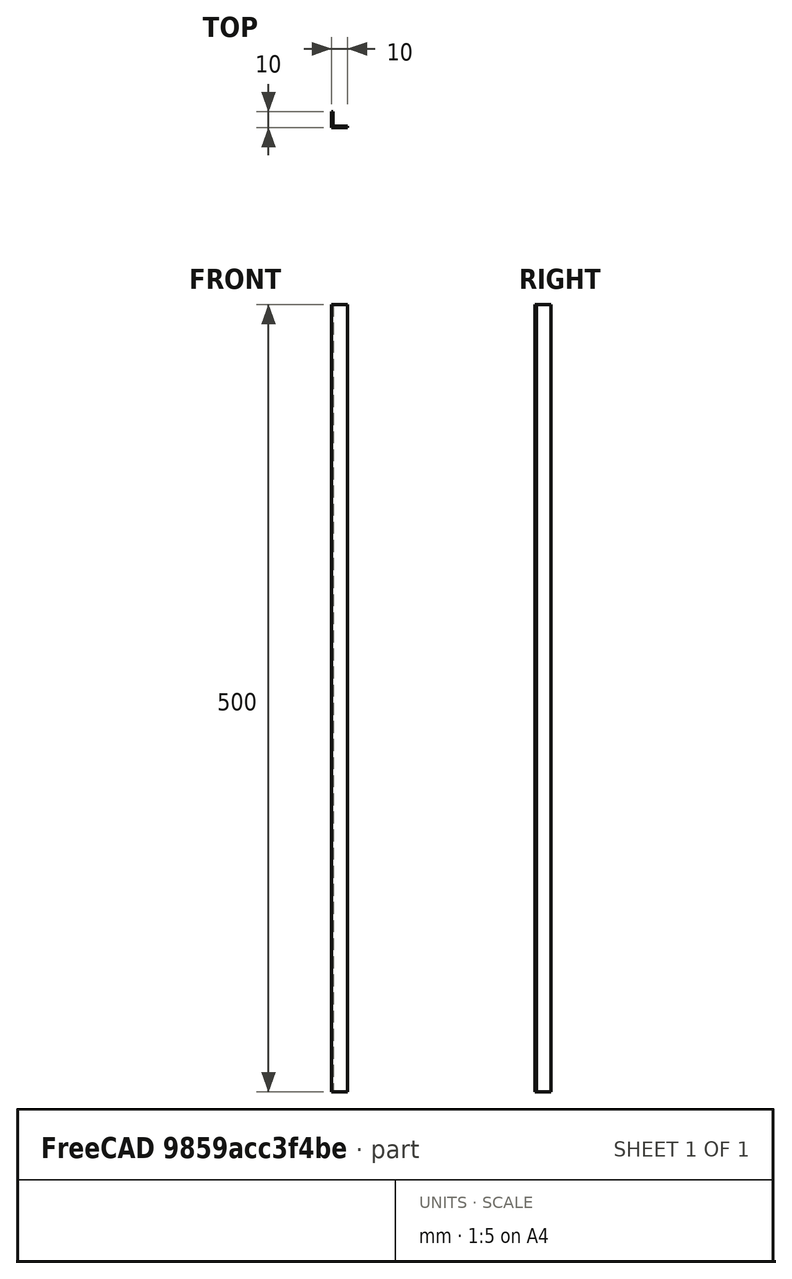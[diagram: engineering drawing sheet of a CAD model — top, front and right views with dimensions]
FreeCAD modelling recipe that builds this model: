
FCSTD DOCUMENT  (FreeCAD 0.18R16131 (Git))
Label: norm_L-profile_10_10_1_500
License: All rights reserved
LicenseURL: http://en.wikipedia.org/wiki/All_rights_reserved
objects: Sketcher::SketchObject×1, PartDesign::Pad×1, PartDesign::Body×1, Spreadsheet::Sheet×1
note: 4 computed .brp shape members not serialized (recipe doc carries the construction recipe); baked Part::Feature solids carry a one-line shape summary decoded from their .brp

FEATURE [Sketcher::SketchObject] Sketch
  MapMode = 5
  Support = -> [XY_Plane]
  expr: Constraints[17] = Lprofile.t1
  expr: Constraints[14] = Lprofile.d2
  expr: Constraints[16] = Lprofile.d1
  sketch-geometry (6):
    g0: LineSegment StartX=0 StartY=0 StartZ=0 EndX=0 EndY=9 EndZ=0
    g1: LineSegment StartX=0 StartY=9 StartZ=0 EndX=-1 EndY=9 EndZ=0
    g2: LineSegment StartX=-1 StartY=9 StartZ=0 EndX=-1 EndY=-1 EndZ=0
    g3: LineSegment StartX=-1 StartY=-1 StartZ=0 EndX=9 EndY=-1 EndZ=0
    g4: LineSegment StartX=9 StartY=-1 StartZ=0 EndX=9 EndY=0 EndZ=0
    g5: LineSegment StartX=9 StartY=0 StartZ=0 EndX=0 EndY=0 EndZ=0
  constraints (18):
    c: PointOnObject(g0,g-2)
    c: Vertical(g0)
    c: Coincident(g1,g0)
    c: Horizontal(g1)
    c: Coincident(g2,g1)
    c: Vertical(g2)
    c: Coincident(g3,g2)
    c: Horizontal(g3)
    c: PointOnObject(g4,g-1)
    c: Vertical(g4)
    c: Coincident(g5,g4)
    c: Coincident(g5,g0)
    c: Horizontal(g5)
    c: Equal(g1,g4)
    c: DistanceX(g3,g3) = 10
    c: Coincident(g3,g4)
    c: DistanceY(g2,g2) = 10
    c: DistanceY(g4,g4) = 1
FEATURE [PartDesign::Pad] Pad
  Length = 500
  Length2 = 100
  Profile = -> Sketch
  Reversed = true
  Type = 0
  expr: Length = Lprofile.l1
FEATURE [PartDesign::Body] Body
  Group = -> [Sketch,Pad]
  Origin = -> Origin
  Tip = -> Pad
FEATURE [Spreadsheet::Sheet] Spreadsheet  label="Lprofile"
  cells = B3=L -Profile; B4=d1; C4(d1)=10; D4=mm; B5=d2; C5(d2)=10; D5=mm; B6=t1; C6(t1)=1; D6=mm; B7=l1; C7(l1)=500; D7=mm
